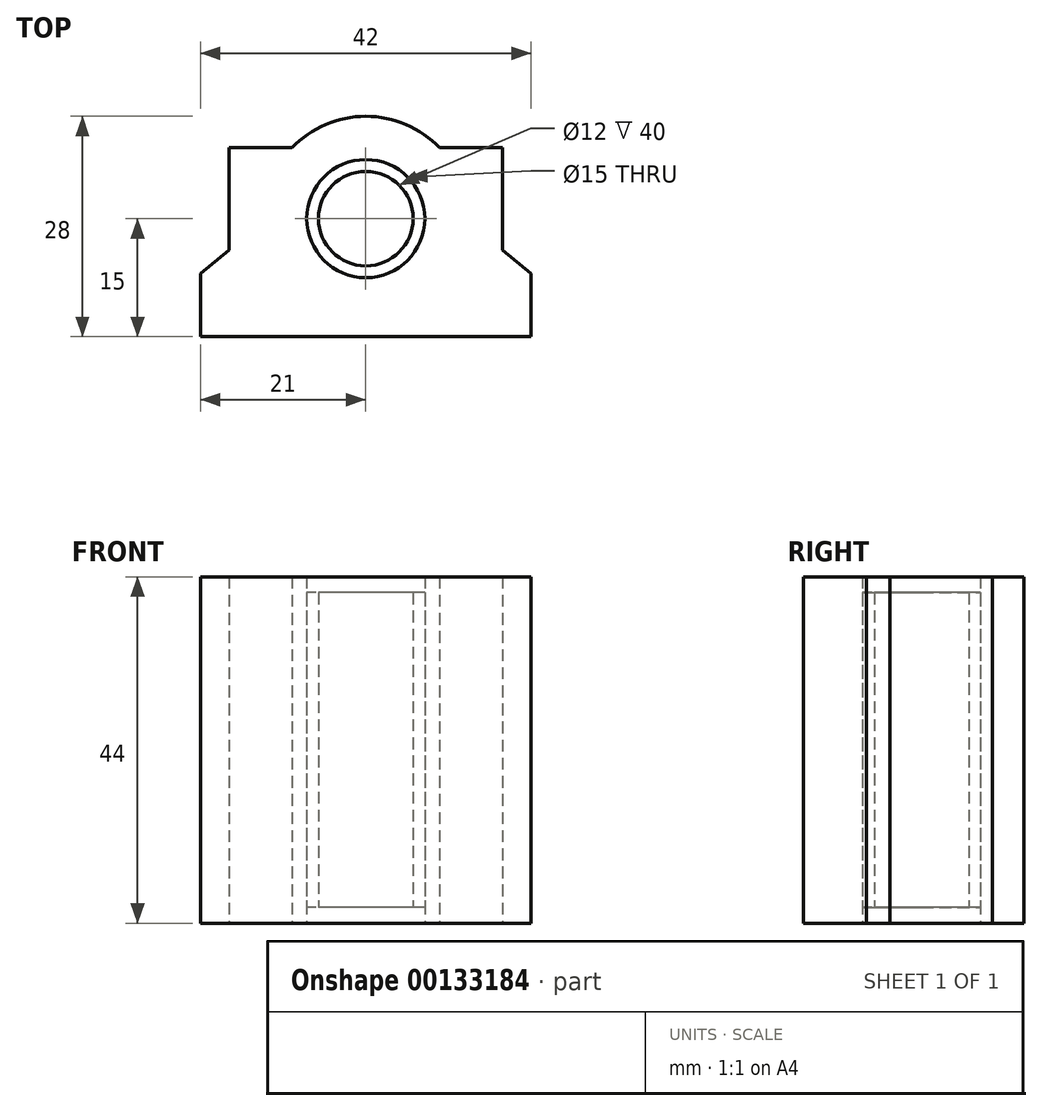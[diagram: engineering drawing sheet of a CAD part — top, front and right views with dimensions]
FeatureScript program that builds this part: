
annotation { "Feature Type Name" : "Feature", "Feature Type Description" : "" }
export const myFeature = defineFeature(function(context is Context, id is Id, definition is map)
    precondition{}
    {
        {
            var Q0;
            Q0=qCreatedBy(makeId("Top.planeOp"),FACE);
            var sketch = newSketch(context, id + "F0", { "sketchPlane" : qUnion([Q0])});
            skLineSegment(sketch, "E0", {"start": v(0, -15) * mm, "end": v(-21, -15) * mm});
            skLineSegment(sketch, "E1", {"start": v(-21, -15) * mm, "end": v(-21, -7) * mm});
            skLineSegment(sketch, "E2", {"start": v(-21, -7) * mm, "end": v(-17.38, -4) * mm});
            skLineSegment(sketch, "E3", {"start": v(-17.38, -4) * mm, "end": v(-17.38, 9) * mm});
            skLineSegment(sketch, "E4", {"start": v(-17.38, 9) * mm, "end": v(-9.38, 9) * mm});
            skArc(sketch, "E5", {"start": v(0, 6) * mm, "mid": v(-6, 0) * mm, "end": v(0, -6) * mm});
            skArc(sketch, "E6.trimOffspring", {"start": v(0, 13) * mm, "mid": v(-5.1, 11.96) * mm, "end": v(-9.38, 9) * mm});
            skArc(sketch, "E7.0", {"start": v(0, 7.5) * mm, "mid": v(-7.5, 0) * mm, "end": v(0, -7.5) * mm});
            skLineSegment(sketch, "E8.MirrorCS", {"start": v(21, -7) * mm, "end": v(17.38, -4) * mm});
            skLineSegment(sketch, "E9.MirrorCS", {"start": v(17.38, 9) * mm, "end": v(9.38, 9) * mm});
            skArc(sketch, "E10.MirrorCS", {"start": v(0, 7.5) * mm, "mid": v(7.5, 0) * mm, "end": v(0, -7.5) * mm});
            skLineSegment(sketch, "E11.MirrorCS", {"start": v(17.38, -4) * mm, "end": v(17.38, 9) * mm});
            skArc(sketch, "E12.MirrorCS", {"start": v(0, 13) * mm, "mid": v(5.1, 11.96) * mm, "end": v(9.38, 9) * mm});
            skArc(sketch, "E13.MirrorCS", {"start": v(0, 6) * mm, "mid": v(6, 0) * mm, "end": v(0, -6) * mm});
            skLineSegment(sketch, "E14.MirrorCS", {"start": v(0, -15) * mm, "end": v(21, -15) * mm});
            skLineSegment(sketch, "E15.MirrorCS", {"start": v(21, -15) * mm, "end": v(21, -7) * mm});
            skSolve(sketch);
        }
        {
            var Q0;
            Q0=makeQuery(id+"F0.imprint","IMPRINT",FACE,{"disambiguationData":[TD([[makeQuery(id+"F0.imprint","IMPRINT",EDGE,{"derivedFrom":sQuery(id+"F0.wireOp",EDGE,"E0")}),-1.0]])]});
            extrude(context, id + "F1", {"entities" : qUnion([Q0]), "depth" : 44 * mm});
        }
        {
            var Q0;
            Q0=makeQuery(id+"F1.opExtrude","CAP_FACE",FACE,{"disambiguationData":[OSD([sQuery(id+"F0.wireOp",EDGE,"E0"),sQuery(id+"F0.wireOp",EDGE,"E1"),sQuery(id+"F0.wireOp",EDGE,"E2"),sQuery(id+"F0.wireOp",EDGE,"E3"),sQuery(id+"F0.wireOp",EDGE,"E4"),sQuery(id+"F0.wireOp",EDGE,"E6.trimOffspring"),sQuery(id+"F0.wireOp",EDGE,"E7.0"),sQuery(id+"F0.wireOp",EDGE,"E8.MirrorCS"),sQuery(id+"F0.wireOp",EDGE,"E9.MirrorCS"),sQuery(id+"F0.wireOp",EDGE,"E10.MirrorCS"),sQuery(id+"F0.wireOp",EDGE,"E11.MirrorCS"),sQuery(id+"F0.wireOp",EDGE,"E12.MirrorCS"),sQuery(id+"F0.wireOp",EDGE,"E14.MirrorCS"),sQuery(id+"F0.wireOp",EDGE,"E15.MirrorCS")])],"isStart":false});
            cPlane(context, id + "F2", {"entities" : qUnion([Q0]), "cplaneType" : CPlaneType.OFFSET, "offset" : 2 * mm, "oppositeDirection" : true, "width" : 150 * mm, "height" : 150 * mm});
        }
        {
            var Q0;
            Q0=makeQuery(id+"F0.imprint","IMPRINT",FACE,{"disambiguationData":[TD([[makeQuery(id+"F0.imprint","IMPRINT",EDGE,{"derivedFrom":sQuery(id+"F0.wireOp",EDGE,"E5")}),-1.0]])]});
            var Q1;
            Q1=qCreatedBy(id+"F2.planeOp",FACE);
            extrude(context, id + "F3", {"entities" : qUnion([Q0]), "endBound" : BoundingType.UP_TO_SURFACE, "endBoundEntityFace" : qUnion([Q1]), "depth" : 30 * mm, "hasSecondDirection" : true, "secondDirectionOppositeDirection" : false, "secondDirectionDepth" : 2 * mm});
        }
    });
